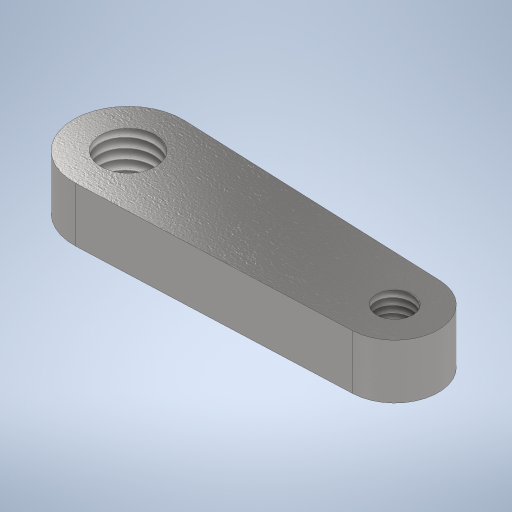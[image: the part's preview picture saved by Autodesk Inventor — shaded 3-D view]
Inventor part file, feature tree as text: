
AUTODESK INVENTOR PART (.ipt)
format: ipt  version: 2024 (Build 280153000, 153)  size: 293,888 bytes
history: native  units: mm
features: sketch x3, hole x2, extrude x1
ambient origin geometry x8: Origin, YZ Plane, XZ Plane, XY Plane, X Axis, Y Axis, Z Axis, Center Point
bodies: Volumenkörper1 (feature_tree)
feature tree (6):
  extrude  "Extrusion1"  Depth=16.0mm
  hole  "Bohrung1"  [1 undecoded]
  hole  "Bohrung2"  [1 undecoded]
  sketch  "Skizze1"  dims[d0=20.0mm d1=16.0mm]
  sketch  "Skizze2"  dims[d2=67.0mm d3=10.0mm d4=0.0mm]
  sketch  "Skizze3"  dims[d5=10.106mm d6=10.0mm d7=4.0mm d8=2.0mm d9=90.0deg d10=8.0mm d11=20.594885mm d12=6.647mm d13=10.0mm d14=4.0mm d15=2.0mm d16=90.0deg d17=8.0mm d18=20.594885mm]
note: 2 required parameter values undecoded (feature->parameter linkage not recoverable at this tier; creation-order binding heuristic only, values carry confidence <= 0.55)
